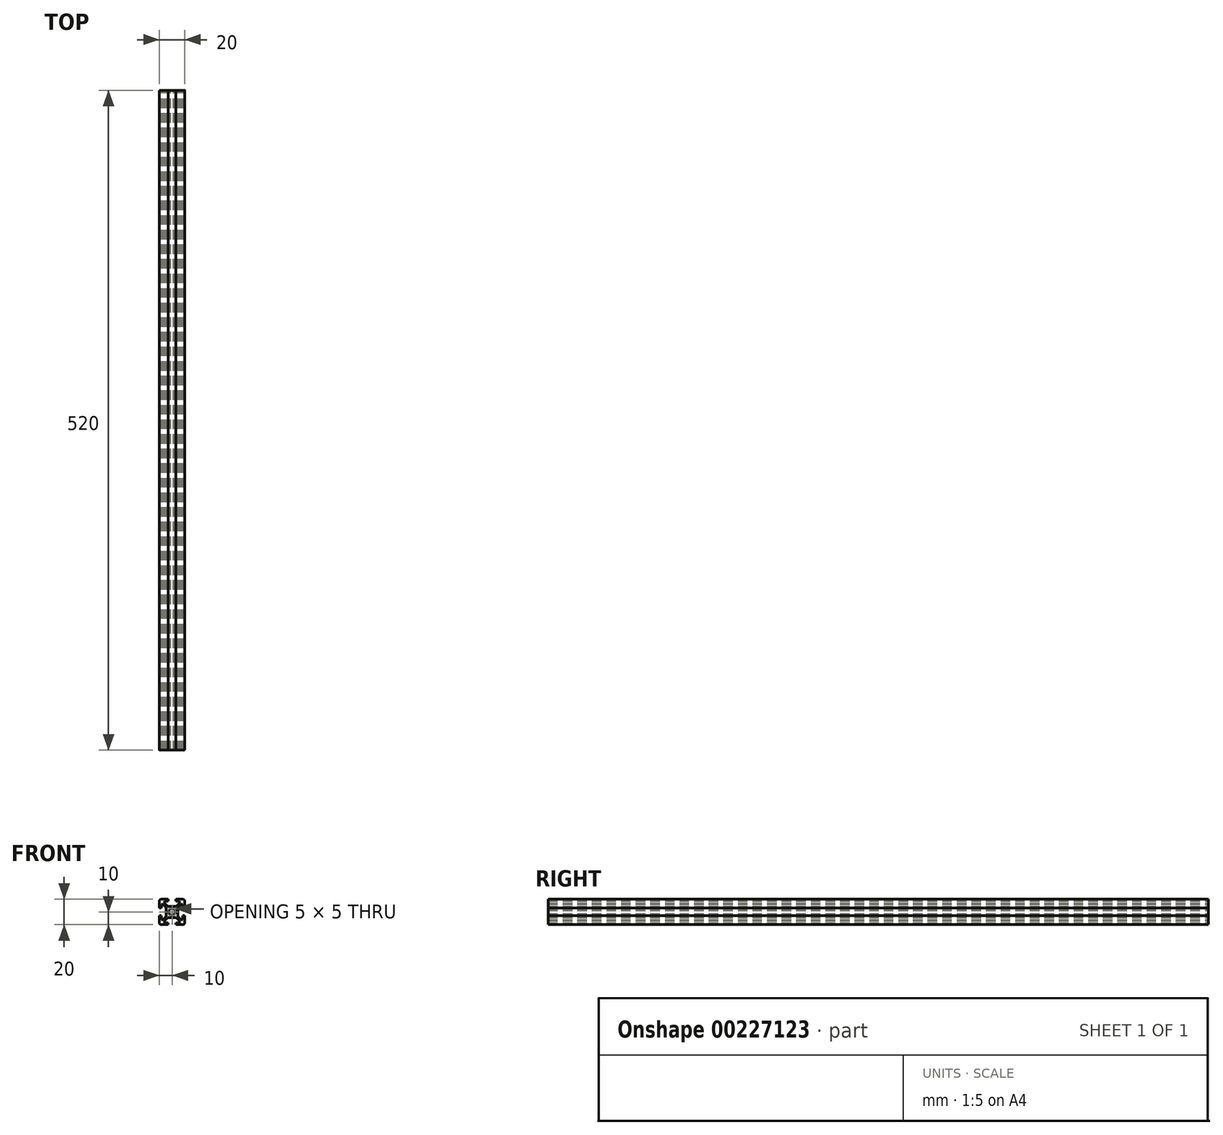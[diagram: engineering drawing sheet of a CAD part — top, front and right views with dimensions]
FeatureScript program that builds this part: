
annotation { "Feature Type Name" : "Feature", "Feature Type Description" : "" }
export const myFeature = defineFeature(function(context is Context, id is Id, definition is map)
    precondition{}
    {
        {
            var Q0;
            Q0=qCreatedBy(makeId("Front.planeOp"),FACE);
            var sketch = newSketch(context, id + "F0", { "sketchPlane" : qUnion([Q0])});
            skLineSegment(sketch, "E0.bottom", {"start": v(8.5, -10) * mm, "end": v(3, -10) * mm});
            skLineSegment(sketch, "E0.top", {"start": v(8.5, 10) * mm, "end": v(3, 10) * mm});
            skLineSegment(sketch, "E0.left", {"start": v(10, -8.5) * mm, "end": v(10, -3) * mm});
            skLineSegment(sketch, "E0.right", {"start": v(-10, -8.5) * mm, "end": v(-10, -3) * mm});
            skPoint(sketch, "E0.middle", {"position": v(0, 0) * mm});
            skLineSegment(sketch, "E1.bottom", {"start": v(6, -8.5) * mm, "end": v(3, -8.5) * mm});
            skLineSegment(sketch, "E1.top", {"start": v(6, 8.5) * mm, "end": v(3, 8.5) * mm});
            skLineSegment(sketch, "E1.left", {"start": v(8.5, -6) * mm, "end": v(8.5, -3) * mm});
            skLineSegment(sketch, "E1.right", {"start": v(-8.5, -6) * mm, "end": v(-8.5, -3) * mm});
            skLineSegment(sketch, "E2.bottom", {"start": v(3.44, -4.5) * mm, "end": v(-3.44, -4.5) * mm});
            skLineSegment(sketch, "E2.top", {"start": v(3.44, 4.5) * mm, "end": v(-3.44, 4.5) * mm});
            skLineSegment(sketch, "E2.left", {"start": v(4.5, -3.44) * mm, "end": v(4.5, 3.44) * mm});
            skLineSegment(sketch, "E2.right", {"start": v(-4.5, -3.44) * mm, "end": v(-4.5, 3.44) * mm});
            skLineSegment(sketch, "E3.bottom", {"start": v(8.5, -6) * mm, "end": v(7.06, -6) * mm});
            skLineSegment(sketch, "E3.top", {"start": v(8.5, 6) * mm, "end": v(7.06, 6) * mm});
            skLineSegment(sketch, "E4.left", {"start": v(6, -8.5) * mm, "end": v(6, -7.06) * mm});
            skLineSegment(sketch, "E4.right", {"start": v(-6, -8.5) * mm, "end": v(-6, -7.06) * mm});
            skPoint(sketch, "E5.orphan", {"position": v(-8.5, 8.5) * mm});
            skPoint(sketch, "E6.orphan", {"position": v(8.5, 8.5) * mm});
            skPoint(sketch, "E7.orphan", {"position": v(8.5, -8.5) * mm});
            skPoint(sketch, "E8.orphan", {"position": v(-8.5, -8.5) * mm});
            skLineSegment(sketch, "E9.trimOffspring", {"start": v(-6, 7.06) * mm, "end": v(-6, 8.5) * mm});
            skLineSegment(sketch, "E10.trimOffspring", {"start": v(-7.06, 6) * mm, "end": v(-8.5, 6) * mm});
            skLineSegment(sketch, "E11.trimOffspring", {"start": v(6, 7.06) * mm, "end": v(6, 8.5) * mm});
            skLineSegment(sketch, "E12.trimOffspring", {"start": v(-7.06, -6) * mm, "end": v(-8.5, -6) * mm});
            skLineSegment(sketch, "E13", {"start": v(-10, 10) * mm, "end": v(0, 0) * mm, "construction": true});
            skLineSegment(sketch, "E14", {"start": v(10, 10) * mm, "end": v(0, 0) * mm, "construction": true});
            skLineSegment(sketch, "E15", {"start": v(-6, 7.06) * mm, "end": v(-3.44, 4.5) * mm});
            skPoint(sketch, "E15.endSnap0", {"position": v(7.25, -6) * mm});
            skLineSegment(sketch, "E16", {"start": v(6, -7.06) * mm, "end": v(3.44, -4.5) * mm});
            skLineSegment(sketch, "E17", {"start": v(7.06, 6) * mm, "end": v(4.5, 3.44) * mm});
            skLineSegment(sketch, "E18", {"start": v(6, 7.06) * mm, "end": v(3.44, 4.5) * mm});
            skPoint(sketch, "E19.orphan", {"position": v(6, -6) * mm});
            skPoint(sketch, "E20.orphan", {"position": v(-4.5, -4.5) * mm});
            skPoint(sketch, "E21.orphan", {"position": v(-4.5, 4.5) * mm});
            skPoint(sketch, "E22.orphan", {"position": v(4.5, 4.5) * mm});
            skPoint(sketch, "E23.orphan", {"position": v(4.5, -4.5) * mm});
            skLineSegment(sketch, "E24.trimOffspring", {"start": v(4.5, -3.44) * mm, "end": v(7.06, -6) * mm});
            skLineSegment(sketch, "E25.trimOffspring", {"start": v(-3.44, -4.5) * mm, "end": v(-6, -7.06) * mm});
            skLineSegment(sketch, "E26.trimOffspring", {"start": v(-4.5, -3.44) * mm, "end": v(-7.06, -6) * mm});
            skLineSegment(sketch, "E27.trimOffspring", {"start": v(-4.5, 3.44) * mm, "end": v(-7.06, 6) * mm});
            skLineSegment(sketch, "E28.bottom", {"start": v(8.5, -3) * mm, "end": v(10, -3) * mm});
            skLineSegment(sketch, "E28.top", {"start": v(8.5, 3) * mm, "end": v(10, 3) * mm});
            skPoint(sketch, "E28.middle", {"position": v(10, 0) * mm});
            skLineSegment(sketch, "E29.left", {"start": v(3, 8.5) * mm, "end": v(3, 10) * mm});
            skLineSegment(sketch, "E29.right", {"start": v(-3, 8.5) * mm, "end": v(-3, 10) * mm});
            skPoint(sketch, "E29.middle", {"position": v(0, 10) * mm});
            skLineSegment(sketch, "E30.bottom", {"start": v(-8.5, 3) * mm, "end": v(-10, 3) * mm});
            skLineSegment(sketch, "E30.top", {"start": v(-8.5, -3) * mm, "end": v(-10, -3) * mm});
            skPoint(sketch, "E30.middle", {"position": v(-10, 0) * mm});
            skLineSegment(sketch, "E31.left", {"start": v(3, -8.5) * mm, "end": v(3, -10) * mm});
            skLineSegment(sketch, "E31.right", {"start": v(-3, -8.5) * mm, "end": v(-3, -10) * mm});
            skPoint(sketch, "E31.middle", {"position": v(0, -10) * mm});
            skPoint(sketch, "E32.orphan", {"position": v(3, 11.5) * mm});
            skPoint(sketch, "E33.orphan", {"position": v(-3, 11.5) * mm});
            skLineSegment(sketch, "E34.trimOffspring", {"start": v(-3, 10) * mm, "end": v(-8.5, 10) * mm});
            skLineSegment(sketch, "E35.trimOffspring", {"start": v(-3, 8.5) * mm, "end": v(-6, 8.5) * mm});
            skPoint(sketch, "E28.right.end.orphan", {"position": v(11.5, 3) * mm});
            skPoint(sketch, "E36.orphan", {"position": v(11.5, -3) * mm});
            skLineSegment(sketch, "E37.trimOffspring", {"start": v(10, 3) * mm, "end": v(10, 8.5) * mm});
            skLineSegment(sketch, "E38.trimOffspring", {"start": v(8.5, 3) * mm, "end": v(8.5, 6) * mm});
            skPoint(sketch, "E39.orphan", {"position": v(3, -11.5) * mm});
            skPoint(sketch, "E40.orphan", {"position": v(-3, -11.5) * mm});
            skLineSegment(sketch, "E41.trimOffspring", {"start": v(-3, -10) * mm, "end": v(-8.5, -10) * mm});
            skLineSegment(sketch, "E42.trimOffspring", {"start": v(-3, -8.5) * mm, "end": v(-6, -8.5) * mm});
            skPoint(sketch, "E30.right.end.orphan", {"position": v(-11.5, -3) * mm});
            skPoint(sketch, "E43.orphan", {"position": v(-11.5, 3) * mm});
            skLineSegment(sketch, "E44.trimOffspring", {"start": v(-10, 3) * mm, "end": v(-10, 8.5) * mm});
            skLineSegment(sketch, "E45.trimOffspring", {"start": v(-8.5, 3) * mm, "end": v(-8.5, 6) * mm});
            skLineSegment(sketch, "E46.trimOffspring", {"start": v(0, 0) * mm, "end": v(10, -10) * mm, "construction": true});
            skLineSegment(sketch, "E47.trimOffspring", {"start": v(0, 0) * mm, "end": v(-10, -10) * mm, "construction": true});
            skArc(sketch, "E48", {"start": v(1.16, 2.22) * mm, "mid": v(0, 2.5) * mm, "end": v(-1.16, 2.22) * mm});
            skLineSegment(sketch, "E49", {"start": v(-2.5, -1.44) * mm, "end": v(1.44, 2.5) * mm});
            skLineSegment(sketch, "E50", {"start": v(2.5, 1.44) * mm, "end": v(-1.44, -2.5) * mm});
            skLineSegment(sketch, "E51", {"start": v(1.44, -2.5) * mm, "end": v(-2.5, 1.44) * mm});
            skLineSegment(sketch, "E52", {"start": v(-1.44, 2.5) * mm, "end": v(2.5, -1.44) * mm});
            skLineSegment(sketch, "E53", {"start": v(2.5, 1.44) * mm, "end": v(2.5, -1.44) * mm, "construction": true});
            skLineSegment(sketch, "E54", {"start": v(1.44, -2.5) * mm, "end": v(-1.44, -2.5) * mm, "construction": true});
            skLineSegment(sketch, "E55", {"start": v(-2.5, -1.44) * mm, "end": v(-2.5, 1.44) * mm, "construction": true});
            skLineSegment(sketch, "E56", {"start": v(-1.44, 2.5) * mm, "end": v(1.44, 2.5) * mm, "construction": true});
            skLineSegment(sketch, "E57", {"start": v(-1.44, 2.5) * mm, "end": v(-2.5, 1.44) * mm});
            skLineSegment(sketch, "E58", {"start": v(1.44, 2.5) * mm, "end": v(2.5, 1.44) * mm});
            skLineSegment(sketch, "E59", {"start": v(2.5, -1.44) * mm, "end": v(1.44, -2.5) * mm});
            skLineSegment(sketch, "E60", {"start": v(-1.44, -2.5) * mm, "end": v(-2.5, -1.44) * mm});
            skArc(sketch, "E61.trimOffspring", {"start": v(-2.22, 1.16) * mm, "mid": v(-2.5, 0) * mm, "end": v(-2.22, -1.16) * mm});
            skArc(sketch, "E62.trimOffspring", {"start": v(-1.16, -2.22) * mm, "mid": v(0, -2.5) * mm, "end": v(1.16, -2.22) * mm});
            skArc(sketch, "E63.trimOffspring", {"start": v(2.22, -1.16) * mm, "mid": v(2.5, 0) * mm, "end": v(2.22, 1.16) * mm});
            skPoint(sketch, "E64.visualSharp", {"position": v(10, 10) * mm});
            skArc(sketch, "E64.filletArc", {"start": v(10, 8.5) * mm, "mid": v(9.56, 9.56) * mm, "end": v(8.5, 10) * mm});
            skPoint(sketch, "E65.visualSharp", {"position": v(10, -10) * mm});
            skArc(sketch, "E65.filletArc", {"start": v(8.5, -10) * mm, "mid": v(9.56, -9.56) * mm, "end": v(10, -8.5) * mm});
            skPoint(sketch, "E66.visualSharp", {"position": v(-10, -10) * mm});
            skArc(sketch, "E66.filletArc", {"start": v(-10, -8.5) * mm, "mid": v(-9.56, -9.56) * mm, "end": v(-8.5, -10) * mm});
            skPoint(sketch, "E67.visualSharp", {"position": v(-10, 10) * mm});
            skArc(sketch, "E67.filletArc", {"start": v(-8.5, 10) * mm, "mid": v(-9.56, 9.56) * mm, "end": v(-10, 8.5) * mm});
            skSolve(sketch);
        }
        {
            assignVariable(context, id + "F2", {"name" : "Length", "anyValue" : 520});
        }
        {
            var Q0;
            Q0=qSketchRegion(id+"F0",true);
            extrude(context, id + "F1", {"entities" : qUnion([Q0]), "depth" : (getVariable(context, 'Length')) * mm});
        }
    });
